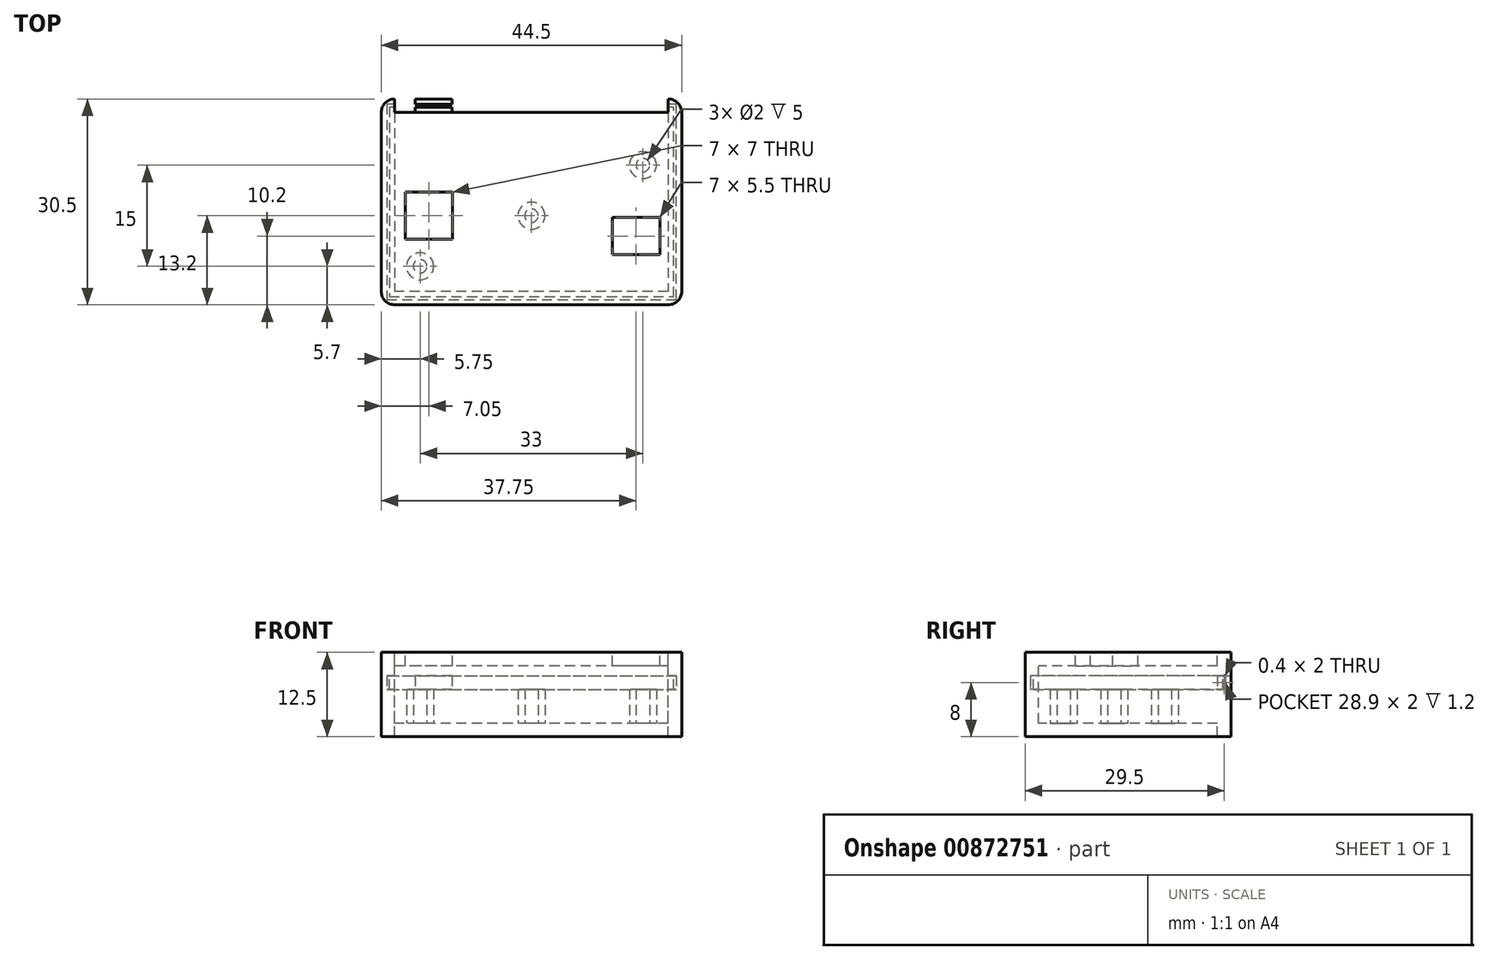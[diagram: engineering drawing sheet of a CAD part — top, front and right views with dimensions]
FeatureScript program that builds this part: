
annotation { "Feature Type Name" : "Feature", "Feature Type Description" : "" }
export const myFeature = defineFeature(function(context is Context, id is Id, definition is map)
    precondition{}
    {
        {
            var Q0;
            Q0=qCreatedBy(makeId("Top.planeOp"),FACE);
            var sketch = newSketch(context, id + "F0", { "sketchPlane" : qUnion([Q0])});
            skLineSegment(sketch, "E0.bottom", {"start": v(20.25, 13.25) * mm, "end": v(-20.25, 13.25) * mm, "construction": true});
            skLineSegment(sketch, "E0.top", {"start": v(20.25, -13.25) * mm, "end": v(-20.25, -13.25) * mm, "construction": true});
            skLineSegment(sketch, "E0.left", {"start": v(20.25, 13.25) * mm, "end": v(20.25, -13.25) * mm, "construction": true});
            skLineSegment(sketch, "E0.right", {"start": v(-20.25, 13.25) * mm, "end": v(-20.25, -13.25) * mm, "construction": true});
            skPoint(sketch, "E0.middle", {"position": v(0, 0) * mm});
            skLineSegment(sketch, "E1.bottom", {"start": v(22.25, 15.25) * mm, "end": v(-22.25, 15.25) * mm});
            skLineSegment(sketch, "E1.top", {"start": v(22.25, -15.25) * mm, "end": v(-22.25, -15.25) * mm});
            skLineSegment(sketch, "E1.left", {"start": v(22.25, 15.25) * mm, "end": v(22.25, -15.25) * mm});
            skLineSegment(sketch, "E1.right", {"start": v(-22.25, 15.25) * mm, "end": v(-22.25, -15.25) * mm});
            skCircle(sketch, "E2", {"center": v(0, -2.05) * mm, "radius": 1.75 * mm, "construction": true});
            skPoint(sketch, "E2.centerSnap0", {"position": v(0, -15.25) * mm});
            skCircle(sketch, "E3", {"center": v(16.5, 5.45) * mm, "radius": 1.25 * mm, "construction": true});
            skCircle(sketch, "E4", {"center": v(-16.5, -9.55) * mm, "radius": 1.25 * mm, "construction": true});
            skLineSegment(sketch, "E5.bottom", {"start": v(-11.7, -5.55) * mm, "end": v(-18.7, -5.55) * mm, "construction": true});
            skLineSegment(sketch, "E5.top", {"start": v(-11.7, 1.45) * mm, "end": v(-18.7, 1.45) * mm, "construction": true});
            skLineSegment(sketch, "E5.left", {"start": v(-11.7, -5.55) * mm, "end": v(-11.7, 1.45) * mm, "construction": true});
            skLineSegment(sketch, "E5.right", {"start": v(-18.7, -5.55) * mm, "end": v(-18.7, 1.45) * mm, "construction": true});
            skPoint(sketch, "E5.middle", {"position": v(-15.2, -2.05) * mm});
            skLineSegment(sketch, "E6.bottom", {"start": v(19, -7.8) * mm, "end": v(12, -7.8) * mm, "construction": true});
            skLineSegment(sketch, "E6.top", {"start": v(19, -2.3) * mm, "end": v(12, -2.3) * mm, "construction": true});
            skLineSegment(sketch, "E6.left", {"start": v(19, -7.8) * mm, "end": v(19, -2.3) * mm, "construction": true});
            skLineSegment(sketch, "E6.right", {"start": v(12, -7.8) * mm, "end": v(12, -2.3) * mm, "construction": true});
            skPoint(sketch, "E6.middle", {"position": v(15.5, -5.05) * mm});
            skSolve(sketch);
        }
        {
            var Q0;
            Q0=makeQuery(id+"F0.imprint","IMPRINT",FACE,{"disambiguationData":[TD([[makeQuery(id+"F0.imprint","IMPRINT",EDGE,{"derivedFrom":sQuery(id+"F0.wireOp",EDGE,"E1.bottom")}),1.0]])]});
            extrude(context, id + "F1", {"entities" : qUnion([Q0]), "oppositeDirection" : true, "depth" : 7 * mm, "offsetDistance" : 25 * mm});
        }
        {
            var Q0;
            Q0=makeQuery(id+"F1.opExtrude","CAP_FACE",FACE,{"disambiguationData":[OSD([sQuery(id+"F0.wireOp",EDGE,"E1.bottom"),sQuery(id+"F0.wireOp",EDGE,"E1.top"),sQuery(id+"F0.wireOp",EDGE,"E1.left"),sQuery(id+"F0.wireOp",EDGE,"E1.right")])],"isStart":true});
            shell(context, id + "F2", {"entities" : qUnion([Q0]), "thickness" : 2 * mm});
        }
        {
            var Q0;
            Q0 = qSketchRegion(id + "F0", true);
            extrude(context, id + "F3", {"entities" : qUnion([Q0]), "depth" : 5.5 * mm, "offsetDistance" : 25 * mm});
        }
        {
            var Q0;
            Q0=makeQuery(id+"F3.opExtrude","CAP_FACE",FACE,{"disambiguationData":[OSD([sQuery(id+"F0.wireOp",EDGE,"E1.bottom"),sQuery(id+"F0.wireOp",EDGE,"E1.top"),sQuery(id+"F0.wireOp",EDGE,"E1.left"),sQuery(id+"F0.wireOp",EDGE,"E1.right")])],"isStart":true});
            shell(context, id + "F4", {"entities" : qUnion([Q0]), "thickness" : 2 * mm});
        }
        {
            var Q0;
            Q0=qCreatedBy(makeId("Right.planeOp"),FACE);
            var sketch = newSketch(context, id + "F5", { "sketchPlane" : qUnion([Q0])});
            skLineSegment(sketch, "E7.bottom", {"start": v(-15.25, 0) * mm, "end": v(-14.45, 0) * mm});
            skLineSegment(sketch, "E7.top", {"start": v(-15.25, 2) * mm, "end": v(-14.45, 2) * mm});
            skLineSegment(sketch, "E7.left", {"start": v(-15.25, 0) * mm, "end": v(-15.25, 2) * mm});
            skLineSegment(sketch, "E7.right", {"start": v(-14.45, 0) * mm, "end": v(-14.45, 2) * mm});
            skLineSegment(sketch, "E8.bottom", {"start": v(-14.05, 0) * mm, "end": v(-13.25, 0) * mm});
            skLineSegment(sketch, "E8.top", {"start": v(-14.05, 2) * mm, "end": v(-13.25, 2) * mm});
            skLineSegment(sketch, "E8.left", {"start": v(-14.05, 0) * mm, "end": v(-14.05, 2) * mm});
            skLineSegment(sketch, "E8.right", {"start": v(-13.25, 0) * mm, "end": v(-13.25, 2) * mm});
            skSolve(sketch);
        }
        {
            var Q0;
            Q0 = qSketchRegion(id + "F0", true);
            extrude(context, id + "F6", {"entities" : qUnion([Q0]), "operationType" : NewBodyOperationType.REMOVE, "depth" : 2 * mm, "offsetDistance" : 25 * mm});
        }
        {
            var Q0;
            Q0=makeQuery(id+"F5.imprint","IMPRINT",FACE,{"disambiguationData":[TD([[makeQuery(id+"F5.imprint","IMPRINT",EDGE,{"derivedFrom":sQuery(id+"F5.wireOp",EDGE,"E8.bottom")}),1.0]])]});
            var Q1;
            {var subQ0=sQuery(id+"F0.wireOp",EDGE,"E1.top");Q1=makeQuery(id+"F6.boolean.opBoolean","INTERSECT",EDGE,{"derivedFrom":[makeQuery(id+"F4.opShell","OFFSET_FACE",FACE,{"disambiguationData":[OSD([subQ0])]}),makeQuery(id+"F6.opExtrude","CAP_FACE",FACE,{"disambiguationData":[OSD([sQuery(id+"F0.wireOp",EDGE,"E1.bottom"),subQ0,sQuery(id+"F0.wireOp",EDGE,"E1.left"),sQuery(id+"F0.wireOp",EDGE,"E1.right")])],"isStart":false})]});}
            var Q2;
            {var subQ0=sQuery(id+"F0.wireOp",EDGE,"E1.left");Q2=makeQuery(id+"F6.boolean.opBoolean","INTERSECT",EDGE,{"derivedFrom":[makeQuery(id+"F4.opShell","OFFSET_FACE",FACE,{"disambiguationData":[OSD([subQ0])]}),makeQuery(id+"F6.opExtrude","CAP_FACE",FACE,{"disambiguationData":[OSD([sQuery(id+"F0.wireOp",EDGE,"E1.bottom"),sQuery(id+"F0.wireOp",EDGE,"E1.top"),subQ0,sQuery(id+"F0.wireOp",EDGE,"E1.right")])],"isStart":false})]});}
            var Q3;
            {var subQ0=sQuery(id+"F0.wireOp",EDGE,"E1.bottom");Q3=makeQuery(id+"F6.boolean.opBoolean","INTERSECT",EDGE,{"derivedFrom":[makeQuery(id+"F4.opShell","OFFSET_FACE",FACE,{"disambiguationData":[OSD([subQ0])]}),makeQuery(id+"F6.opExtrude","CAP_FACE",FACE,{"disambiguationData":[OSD([subQ0,sQuery(id+"F0.wireOp",EDGE,"E1.top"),sQuery(id+"F0.wireOp",EDGE,"E1.left"),sQuery(id+"F0.wireOp",EDGE,"E1.right")])],"isStart":false})]});}
            var Q4;
            {var subQ0=sQuery(id+"F0.wireOp",EDGE,"E1.right");Q4=makeQuery(id+"F6.boolean.opBoolean","INTERSECT",EDGE,{"derivedFrom":[makeQuery(id+"F4.opShell","OFFSET_FACE",FACE,{"disambiguationData":[OSD([subQ0])]}),makeQuery(id+"F6.opExtrude","CAP_FACE",FACE,{"disambiguationData":[OSD([sQuery(id+"F0.wireOp",EDGE,"E1.bottom"),sQuery(id+"F0.wireOp",EDGE,"E1.top"),sQuery(id+"F0.wireOp",EDGE,"E1.left"),subQ0])],"isStart":false})]});}
            sweep(context, id + "F7", {"operationType" : NewBodyOperationType.ADD, "profiles" : qUnion([Q0]), "path" : qUnion([Q1, Q2, Q3, Q4])});
        }
        {
            var Q0;
            Q0=makeQuery(id+"F5.imprint","IMPRINT",FACE,{"disambiguationData":[TD([[makeQuery(id+"F5.imprint","IMPRINT",EDGE,{"derivedFrom":sQuery(id+"F5.wireOp",EDGE,"E7.bottom")}),1.0]])]});
            var Q1;
            Q1=sQuery(id+"F0.wireOp",EDGE,"E1.top");
            var Q2;
            Q2=sQuery(id+"F0.wireOp",EDGE,"E1.left");
            var Q3;
            Q3=sQuery(id+"F0.wireOp",EDGE,"E1.bottom");
            var Q4;
            Q4=sQuery(id+"F0.wireOp",EDGE,"E1.right");
            sweep(context, id + "F8", {"operationType" : NewBodyOperationType.ADD, "profiles" : qUnion([Q0]), "path" : qUnion([Q1, Q2, Q3, Q4])});
        }
        {
            var Q0;
            Q0=makeQuery(id+"F2.opShell","OFFSET_FACE",FACE,{"disambiguationData":[OSD([sQuery(id+"F0.wireOp",EDGE,"E1.bottom"),sQuery(id+"F0.wireOp",EDGE,"E1.top"),sQuery(id+"F0.wireOp",EDGE,"E1.left"),sQuery(id+"F0.wireOp",EDGE,"E1.right")])]});
            var sketch = newSketch(context, id + "F9", { "sketchPlane" : qUnion([Q0])});
            skCircle(sketch, "E9", {"center": v(0, -2.05) * mm, "radius": 2 * mm});
            skCircle(sketch, "E10", {"center": v(-16.5, -9.55) * mm, "radius": 2 * mm});
            skCircle(sketch, "E11", {"center": v(16.5, 5.45) * mm, "radius": 2 * mm});
            skCircle(sketch, "E12", {"center": v(-16.5, -9.55) * mm, "radius": 1 * mm});
            skCircle(sketch, "E13", {"center": v(0, -2.05) * mm, "radius": 1 * mm});
            skCircle(sketch, "E14", {"center": v(16.5, 5.45) * mm, "radius": 1 * mm});
            skSolve(sketch);
        }
        {
            var Q0;
            Q0 = qSketchRegion(id + "F9", true);
            extrude(context, id + "F10", {"entities" : qUnion([Q0]), "operationType" : NewBodyOperationType.ADD, "depth" : 5 * mm, "offsetDistance" : 25 * mm});
        }
        {
            var Q0;
            Q0=makeQuery(id+"F3.opExtrude","CAP_FACE",FACE,{"disambiguationData":[OSD([sQuery(id+"F0.wireOp",EDGE,"E1.bottom"),sQuery(id+"F0.wireOp",EDGE,"E1.top"),sQuery(id+"F0.wireOp",EDGE,"E1.left"),sQuery(id+"F0.wireOp",EDGE,"E1.right")])],"isStart":false});
            var sketch = newSketch(context, id + "F11", { "sketchPlane" : qUnion([Q0])});
            skLineSegment(sketch, "E15.bottom", {"start": v(-18.7, 1.45) * mm, "end": v(-11.7, 1.45) * mm});
            skLineSegment(sketch, "E15.top", {"start": v(-18.7, -5.55) * mm, "end": v(-11.7, -5.55) * mm});
            skLineSegment(sketch, "E15.left", {"start": v(-18.7, 1.45) * mm, "end": v(-18.7, -5.55) * mm});
            skLineSegment(sketch, "E15.right", {"start": v(-11.7, 1.45) * mm, "end": v(-11.7, -5.55) * mm});
            skLineSegment(sketch, "E16.bottom", {"start": v(12, -2.3) * mm, "end": v(19, -2.3) * mm});
            skLineSegment(sketch, "E16.top", {"start": v(12, -7.8) * mm, "end": v(19, -7.8) * mm});
            skLineSegment(sketch, "E16.left", {"start": v(12, -2.3) * mm, "end": v(12, -7.8) * mm});
            skLineSegment(sketch, "E16.right", {"start": v(19, -2.3) * mm, "end": v(19, -7.8) * mm});
            skSolve(sketch);
        }
        {
            var Q0;
            Q0 = qSketchRegion(id + "F11", true);
            extrude(context, id + "F12", {"entities" : qUnion([Q0]), "operationType" : NewBodyOperationType.REMOVE, "endBound" : BoundingType.UP_TO_NEXT, "oppositeDirection" : true, "depth" : 25 * mm, "offsetDistance" : 25 * mm});
        }
        {
            var Q0;
            Q0=makeQuery(id+"F3.opExtrude","SWEPT_EDGE",EDGE,{"disambiguationData":[OSD([sQuery(id+"F0.wireOp",EDGE,"E1.top"),sQuery(id+"F0.wireOp",EDGE,"E1.right")])]});
            var Q1;
            Q1=makeQuery(id+"F3.opExtrude","SWEPT_EDGE",EDGE,{"disambiguationData":[OSD([sQuery(id+"F0.wireOp",EDGE,"E1.bottom"),sQuery(id+"F0.wireOp",EDGE,"E1.right")])]});
            var Q2;
            Q2=makeQuery(id+"F3.opExtrude","SWEPT_EDGE",EDGE,{"disambiguationData":[OSD([sQuery(id+"F0.wireOp",EDGE,"E1.top"),sQuery(id+"F0.wireOp",EDGE,"E1.left")])]});
            var Q3;
            Q3=makeQuery(id+"F3.opExtrude","SWEPT_EDGE",EDGE,{"disambiguationData":[OSD([sQuery(id+"F0.wireOp",EDGE,"E1.bottom"),sQuery(id+"F0.wireOp",EDGE,"E1.left")])]});
            var Q4;
            Q4=makeQuery(id+"F8.boolean.opBoolean","MERGE",EDGE,{"derivedFrom":[makeQuery(id+"F1.opExtrude","SWEPT_EDGE",EDGE,{"disambiguationData":[OSD([sQuery(id+"F0.wireOp",EDGE,"E1.bottom"),sQuery(id+"F0.wireOp",EDGE,"E1.left")])]}),makeQuery(id+"F8.opSweep","MID_CAP_EDGE",EDGE,{"disambiguationData":[OSD([sQuery(id+"F0.wireOp",VERTEX,"E1.bottom.start"),sQuery(id+"F5.wireOp",EDGE,"E7.left")])],"capPos":1.0})]});
            var Q5;
            Q5=makeQuery(id+"F8.boolean.opBoolean","MERGE",EDGE,{"derivedFrom":[makeQuery(id+"F1.opExtrude","SWEPT_EDGE",EDGE,{"disambiguationData":[OSD([sQuery(id+"F0.wireOp",EDGE,"E1.top"),sQuery(id+"F0.wireOp",EDGE,"E1.left")])]}),makeQuery(id+"F8.opSweep","CAP_EDGE",EDGE,{"disambiguationData":[OSD([sQuery(id+"F0.wireOp",VERTEX,"E1.left.end"),sQuery(id+"F5.wireOp",EDGE,"E7.left")])],"isStart":true})]});
            var Q6;
            Q6=makeQuery(id+"F8.boolean.opBoolean","MERGE",EDGE,{"derivedFrom":[makeQuery(id+"F1.opExtrude","SWEPT_EDGE",EDGE,{"disambiguationData":[OSD([sQuery(id+"F0.wireOp",EDGE,"E1.top"),sQuery(id+"F0.wireOp",EDGE,"E1.right")])]}),makeQuery(id+"F8.opSweep","MID_CAP_EDGE",EDGE,{"disambiguationData":[OSD([sQuery(id+"F0.wireOp",VERTEX,"E1.right.end"),sQuery(id+"F5.wireOp",EDGE,"E7.left")])],"capPos":3.0})]});
            var Q7;
            Q7=makeQuery(id+"F8.boolean.opBoolean","MERGE",EDGE,{"derivedFrom":[makeQuery(id+"F1.opExtrude","SWEPT_EDGE",EDGE,{"disambiguationData":[OSD([sQuery(id+"F0.wireOp",EDGE,"E1.bottom"),sQuery(id+"F0.wireOp",EDGE,"E1.right")])]}),makeQuery(id+"F8.opSweep","MID_CAP_EDGE",EDGE,{"disambiguationData":[OSD([sQuery(id+"F0.wireOp",VERTEX,"E1.right.start"),sQuery(id+"F5.wireOp",EDGE,"E7.left")])],"capPos":2.0})]});
            fillet(context, id + "F13", {"entities" : qUnion([Q0, Q1, Q2, Q3, Q4, Q5, Q6, Q7]), "radius" : 2 * mm, "tangentPropagation" : true, "allowEdgeOverflow" : false});
        }
        {
            var Q0;
            {var subQ0=sQuery(id+"F0.wireOp",EDGE,"E1.bottom");Q0=makeQuery(id+"F8.boolean.opBoolean","MERGE",FACE,{"derivedFrom":[makeQuery(id+"F1.opExtrude","SWEPT_FACE",FACE,{"disambiguationData":[OSD([subQ0])]}),makeQuery(id+"F8.opSweep","SWEPT_FACE",FACE,{"disambiguationData":[OSD([subQ0,sQuery(id+"F5.wireOp",EDGE,"E7.left")])]})]});}
            var sketch = newSketch(context, id + "F14", { "sketchPlane" : qUnion([Q0])});
            skLineSegment(sketch, "E17.bottom", {"start": v(17.25, 2) * mm, "end": v(11.75, 2) * mm});
            skLineSegment(sketch, "E17.top", {"start": v(17.25, 0) * mm, "end": v(11.75, 0) * mm});
            skLineSegment(sketch, "E17.left", {"start": v(17.25, 2) * mm, "end": v(17.25, 0) * mm});
            skLineSegment(sketch, "E17.right", {"start": v(11.75, 2) * mm, "end": v(11.75, 0) * mm});
            skSolve(sketch);
        }
        {
            var Q0;
            Q0=makeQuery(id+"F14.imprint","IMPRINT",FACE,{"disambiguationData":[TD([[makeQuery(id+"F14.imprint","IMPRINT",EDGE,{"derivedFrom":sQuery(id+"F14.wireOp",EDGE,"E17.bottom")}),-1.0]])]});
            extrude(context, id + "F15", {"entities" : qUnion([Q0]), "operationType" : NewBodyOperationType.REMOVE, "oppositeDirection" : true, "depth" : 2 * mm, "offsetDistance" : 25 * mm});
        }
    });
